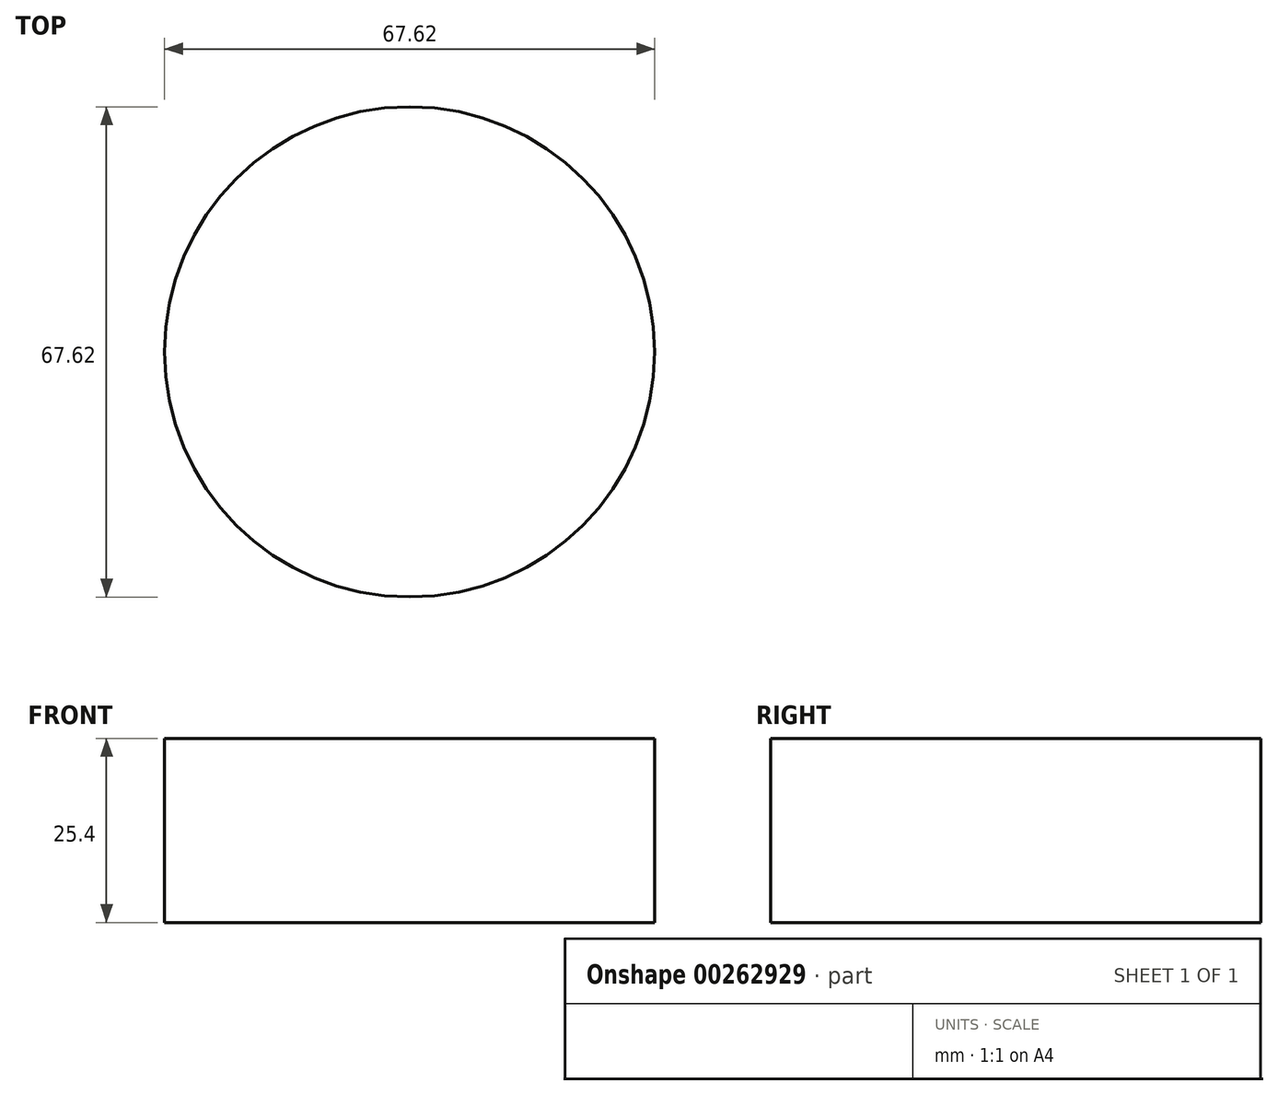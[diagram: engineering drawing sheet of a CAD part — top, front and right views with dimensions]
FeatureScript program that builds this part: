
annotation { "Feature Type Name" : "Feature", "Feature Type Description" : "" }
export const myFeature = defineFeature(function(context is Context, id is Id, definition is map)
    precondition{}
    {
        {
            var Q0;
            Q0=qCreatedBy(makeId("Top.planeOp"),FACE);
            var sketch = newSketch(context, id + "F0", { "sketchPlane" : qUnion([Q0])});
            skCircle(sketch, "E0", {"center": v(0, 0) * mm, "radius": 33.8 * mm});
            skSolve(sketch);
        }
        {
            var Q0;
            Q0 = qSketchRegion(id + "F0", true);
            extrude(context, id + "F1", {"entities" : qUnion([Q0]), "depth" : 25.4 * mm});
        }
    });
